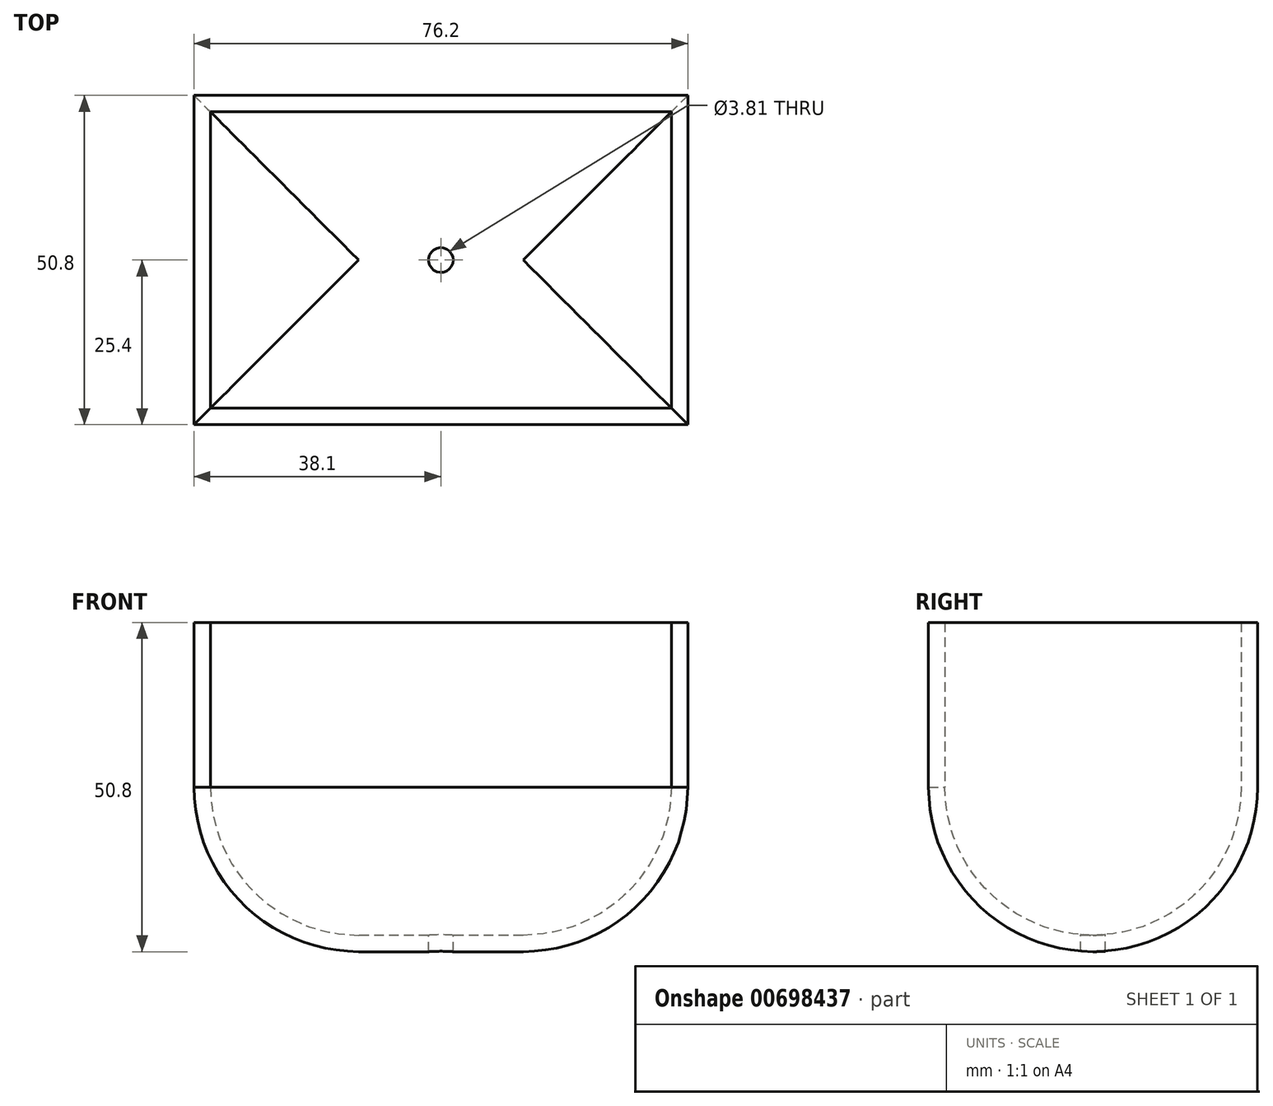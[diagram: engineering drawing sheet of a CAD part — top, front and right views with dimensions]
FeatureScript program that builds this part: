
annotation { "Feature Type Name" : "Feature", "Feature Type Description" : "" }
export const myFeature = defineFeature(function(context is Context, id is Id, definition is map)
    precondition{}
    {
        {
            var Q0;
            Q0=qCreatedBy(makeId("Top.planeOp"),FACE);
            var sketch = newSketch(context, id + "F0", { "sketchPlane" : qUnion([Q0])});
            skLineSegment(sketch, "E0.bottom", {"start": v(-38.1, 25.4) * mm, "end": v(38.1, 25.4) * mm});
            skLineSegment(sketch, "E0.top", {"start": v(-38.1, -25.4) * mm, "end": v(38.1, -25.4) * mm});
            skLineSegment(sketch, "E0.left", {"start": v(-38.1, 25.4) * mm, "end": v(-38.1, -25.4) * mm});
            skLineSegment(sketch, "E0.right", {"start": v(38.1, 25.4) * mm, "end": v(38.1, -25.4) * mm});
            skPoint(sketch, "E0.middle", {"position": v(0, 0) * mm});
            skSolve(sketch);
        }
        {
            var Q0;
            Q0=makeQuery(id+"F0.imprint","IMPRINT",FACE,{"disambiguationData":[TD([[makeQuery(id+"F0.imprint","IMPRINT",EDGE,{"derivedFrom":sQuery(id+"F0.wireOp",EDGE,"E0.bottom")}),-1.0]])]});
            extrude(context, id + "F1", {"entities" : qUnion([Q0]), "depth" : 25.4 * mm, "offsetDistance" : 25.4 * mm});
        }
        {
            var Q0;
            Q0=makeQuery(id+"F1.opExtrude","CAP_FACE",FACE,{"disambiguationData":[OSD([sQuery(id+"F0.wireOp",EDGE,"E0.bottom"),sQuery(id+"F0.wireOp",EDGE,"E0.top"),sQuery(id+"F0.wireOp",EDGE,"E0.left"),sQuery(id+"F0.wireOp",EDGE,"E0.right")])],"isStart":true});
            extrude(context, id + "F2", {"entities" : qUnion([Q0]), "operationType" : NewBodyOperationType.ADD, "depth" : 25.4 * mm, "offsetDistance" : 25.4 * mm});
        }
        {
            var Q0;
            Q0=makeQuery(id+"F2.opExtrude","CAP_EDGE",EDGE,{"disambiguationData":[OSD([sQuery(id+"F0.wireOp",EDGE,"E0.top")])],"isStart":false});
            var Q1;
            Q1=makeQuery(id+"F2.opExtrude","CAP_EDGE",EDGE,{"disambiguationData":[OSD([sQuery(id+"F0.wireOp",EDGE,"E0.right")])],"isStart":false});
            var Q2;
            Q2=makeQuery(id+"F2.opExtrude","CAP_EDGE",EDGE,{"disambiguationData":[OSD([sQuery(id+"F0.wireOp",EDGE,"E0.bottom")])],"isStart":false});
            var Q3;
            Q3=makeQuery(id+"F2.opExtrude","CAP_EDGE",EDGE,{"disambiguationData":[OSD([sQuery(id+"F0.wireOp",EDGE,"E0.left")])],"isStart":false});
            fillet(context, id + "F3", {"entities" : qUnion([Q0, Q1, Q2, Q3]), "radius" : 25.4 * mm, "tangentPropagation" : true, "allowEdgeOverflow" : false});
        }
        {
            var Q0;
            Q0=makeQuery(id+"F1.opExtrude","CAP_FACE",FACE,{"disambiguationData":[OSD([sQuery(id+"F0.wireOp",EDGE,"E0.bottom"),sQuery(id+"F0.wireOp",EDGE,"E0.top"),sQuery(id+"F0.wireOp",EDGE,"E0.left"),sQuery(id+"F0.wireOp",EDGE,"E0.right")])],"isStart":false});
            shell(context, id + "F4", {"entities" : qUnion([Q0]), "thickness" : 2.54 * mm});
        }
        {
            var Q0;
            Q0=qCreatedBy(makeId("Top.planeOp"),FACE);
            var sketch = newSketch(context, id + "F5", { "sketchPlane" : qUnion([Q0])});
            skPoint(sketch, "E1", {"position": v(0, 0) * mm});
            skSolve(sketch);
        }
        {
            var Q0;
            Q0=sQuery(id+"F5.wireOp",VERTEX,"E1");
            var Q1;
            Q1=makeQuery(id+"F1.opExtrude","SWEPT_BODY",BODY,{"disambiguationData":[OSD([sQuery(id+"F0.wireOp",EDGE,"E0.bottom"),sQuery(id+"F0.wireOp",EDGE,"E0.top"),sQuery(id+"F0.wireOp",EDGE,"E0.left"),sQuery(id+"F0.wireOp",EDGE,"E0.right")])]});
            hole(context, id + "F6", {"style" : HoleStyle.SIMPLE, "endStyle" : HoleEndStyle.THROUGH, "holeDiameter" : 3.8 * mm, "majorDiameter" : 6.35 * mm, "isTappedThrough" : true, "tappedDepth" : 12.7 * mm, "tapClearance" : 3, "locations" : qUnion([Q0]), "scope" : qUnion([Q1])});
        }
        {
            var Q0;
            Q0=makeQuery(id+"F1.opExtrude","CAP_FACE",FACE,{"disambiguationData":[OSD([sQuery(id+"F0.wireOp",EDGE,"E0.bottom"),sQuery(id+"F0.wireOp",EDGE,"E0.top"),sQuery(id+"F0.wireOp",EDGE,"E0.left"),sQuery(id+"F0.wireOp",EDGE,"E0.right")])],"isStart":false});
            var sketch = newSketch(context, id + "F7", { "sketchPlane" : qUnion([Q0])});
            skLineSegment(sketch, "E2", {"start": v(-38.1, -25.4) * mm, "end": v(-35.56, -22.86) * mm});
            skLineSegment(sketch, "E3", {"start": v(-35.56, -22.86) * mm, "end": v(35.56, -22.86) * mm});
            skLineSegment(sketch, "E4", {"start": v(35.56, -22.86) * mm, "end": v(38.1, -25.4) * mm});
            skLineSegment(sketch, "E5", {"start": v(38.1, -25.4) * mm, "end": v(-38.1, -25.4) * mm});
            skSolve(sketch);
        }
        {
            var Q0;
            Q0=makeQuery(id+"F7.imprint","IMPRINT",FACE,{"disambiguationData":[TD([[makeQuery(id+"F7.imprint","IMPRINT",EDGE,{"derivedFrom":sQuery(id+"F7.wireOp",EDGE,"E2")}),-1.0]])]});
            extrude(context, id + "F8", {"entities" : qUnion([Q0]), "operationType" : NewBodyOperationType.REMOVE, "oppositeDirection" : true, "depth" : 25.4 * mm, "offsetDistance" : 25.4 * mm});
        }
    });
